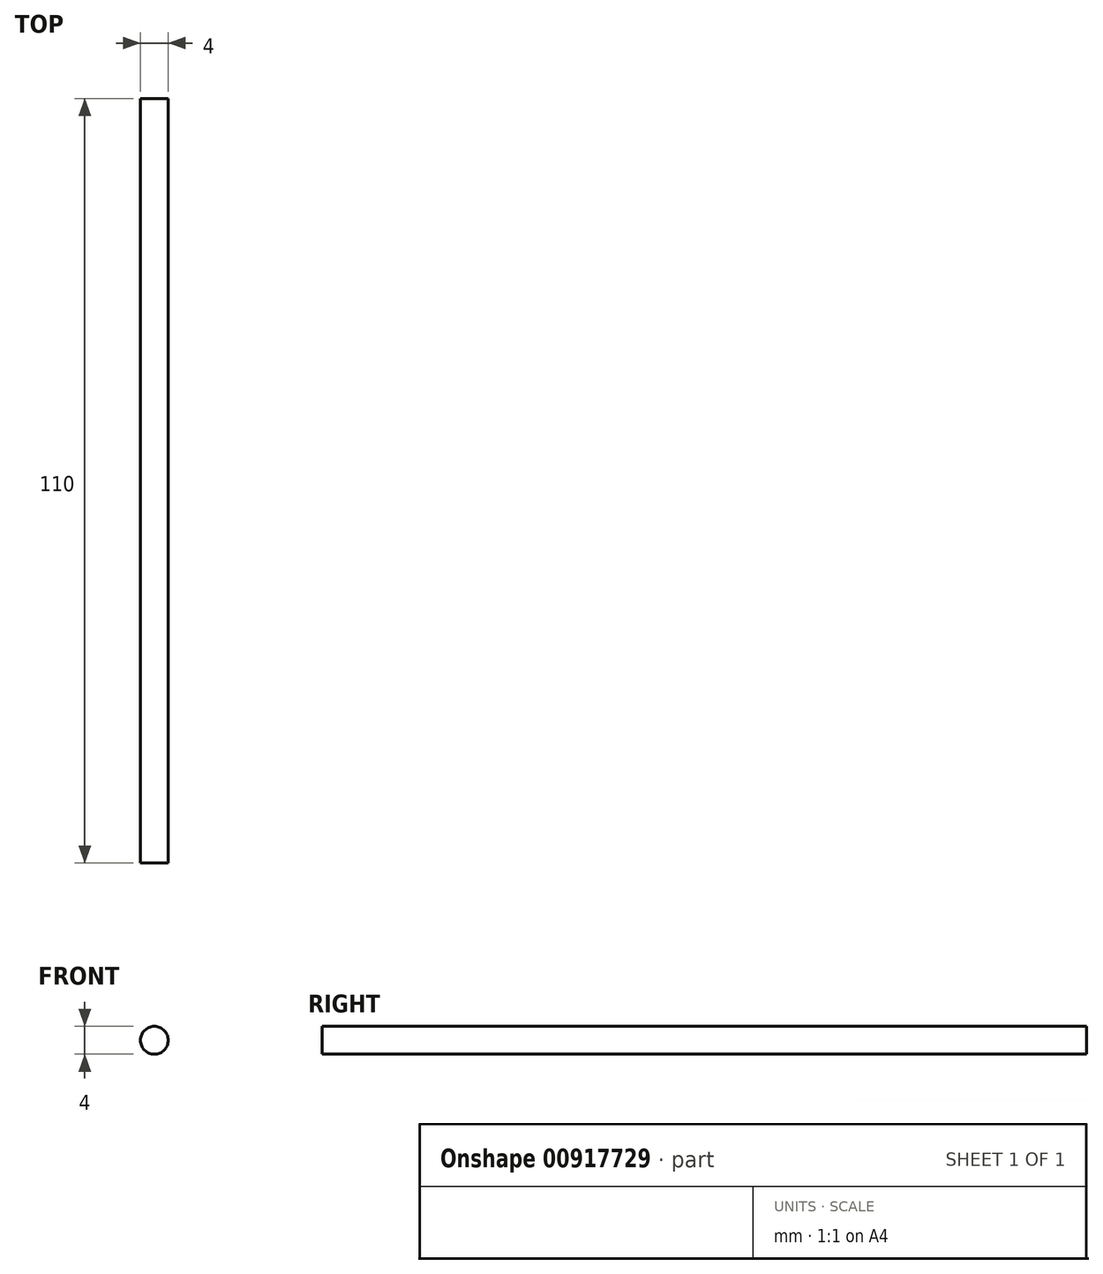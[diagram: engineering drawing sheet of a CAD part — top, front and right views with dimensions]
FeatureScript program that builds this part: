
annotation { "Feature Type Name" : "Feature", "Feature Type Description" : "" }
export const myFeature = defineFeature(function(context is Context, id is Id, definition is map)
    precondition{}
    {
        {
            var Q0;
            Q0=qCreatedBy(makeId("Front.planeOp"),FACE);
            var sketch = newSketch(context, id + "F0", { "sketchPlane" : qUnion([Q0])});
            skCircle(sketch, "E0", {"center": v(0, 0) * mm, "radius": 2 * mm});
            skSolve(sketch);
        }
        {
            var Q0;
            Q0=makeQuery(id+"F0.imprint","IMPRINT",FACE,{"disambiguationData":[TD([[makeQuery(id+"F0.imprint","IMPRINT",EDGE,{"derivedFrom":sQuery(id+"F0.wireOp",EDGE,"E0")}),1.0]])]});
            extrude(context, id + "F1", {"entities" : qUnion([Q0]), "depth" : 110 * mm, "offsetDistance" : 25 * mm, "symmetric" : true});
        }
    });
